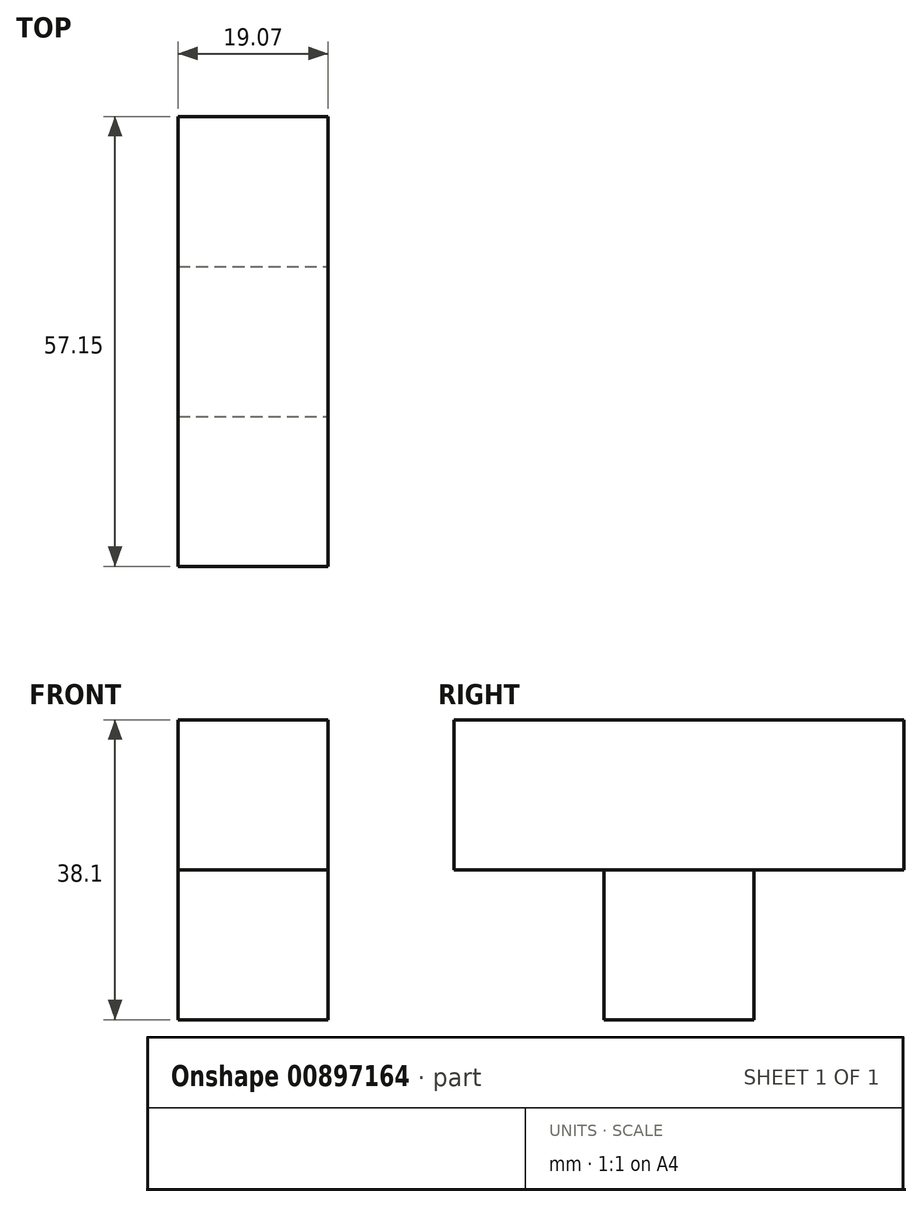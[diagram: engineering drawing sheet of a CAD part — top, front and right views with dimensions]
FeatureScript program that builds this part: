
annotation { "Feature Type Name" : "Feature", "Feature Type Description" : "" }
export const myFeature = defineFeature(function(context is Context, id is Id, definition is map)
    precondition{}
    {
        {
            var Q0;
            Q0=qCreatedBy(makeId("Front.planeOp"),FACE);
            var sketch = newSketch(context, id + "F0", { "sketchPlane" : qUnion([Q0])});
            skLineSegment(sketch, "E0", {"start": v(-9.9, 31.18) * mm, "end": v(9.16, 31.18) * mm});
            skLineSegment(sketch, "E1", {"start": v(-9.9, 31.18) * mm, "end": v(-9.9, 12.13) * mm});
            skLineSegment(sketch, "E2", {"start": v(-9.9, 12.13) * mm, "end": v(9.16, 12.13) * mm});
            skLineSegment(sketch, "E3", {"start": v(9.16, 12.13) * mm, "end": v(9.16, 31.18) * mm});
            skSolve(sketch);
        }
        {
            var Q0;
            Q0 = qSketchRegion(id + "F0", true);
            extrude(context, id + "F1", {"entities" : qUnion([Q0]), "depth" : 38.1 * mm, "offsetDistance" : 25.4 * mm, "hasSecondDirection" : true, "secondDirectionOppositeDirection" : true, "secondDirectionDepth" : 19.05 * mm});
        }
        {
            var Q0;
            Q0=qCreatedBy(makeId("Top.planeOp"),FACE);
            var sketch = newSketch(context, id + "F2", { "sketchPlane" : qUnion([Q0])});
            skLineSegment(sketch, "E4", {"start": v(-9.88, 0) * mm, "end": v(9.17, 0) * mm});
            skLineSegment(sketch, "E5", {"start": v(-9.88, 0) * mm, "end": v(-9.88, -19.05) * mm});
            skLineSegment(sketch, "E6", {"start": v(-9.88, -19.05) * mm, "end": v(9.18, -19.05) * mm});
            skLineSegment(sketch, "E7", {"start": v(9.18, -19.05) * mm, "end": v(9.17, 0) * mm});
            skSolve(sketch);
        }
        {
            var Q0;
            Q0 = qSketchRegion(id + "F2", true);
            extrude(context, id + "F3", {"entities" : qUnion([Q0]), "operationType" : NewBodyOperationType.ADD, "depth" : 12.13 * mm, "offsetDistance" : 25.4 * mm, "hasSecondDirection" : true, "secondDirectionOppositeDirection" : true, "secondDirectionDepth" : 6.92 * mm});
        }
    });
